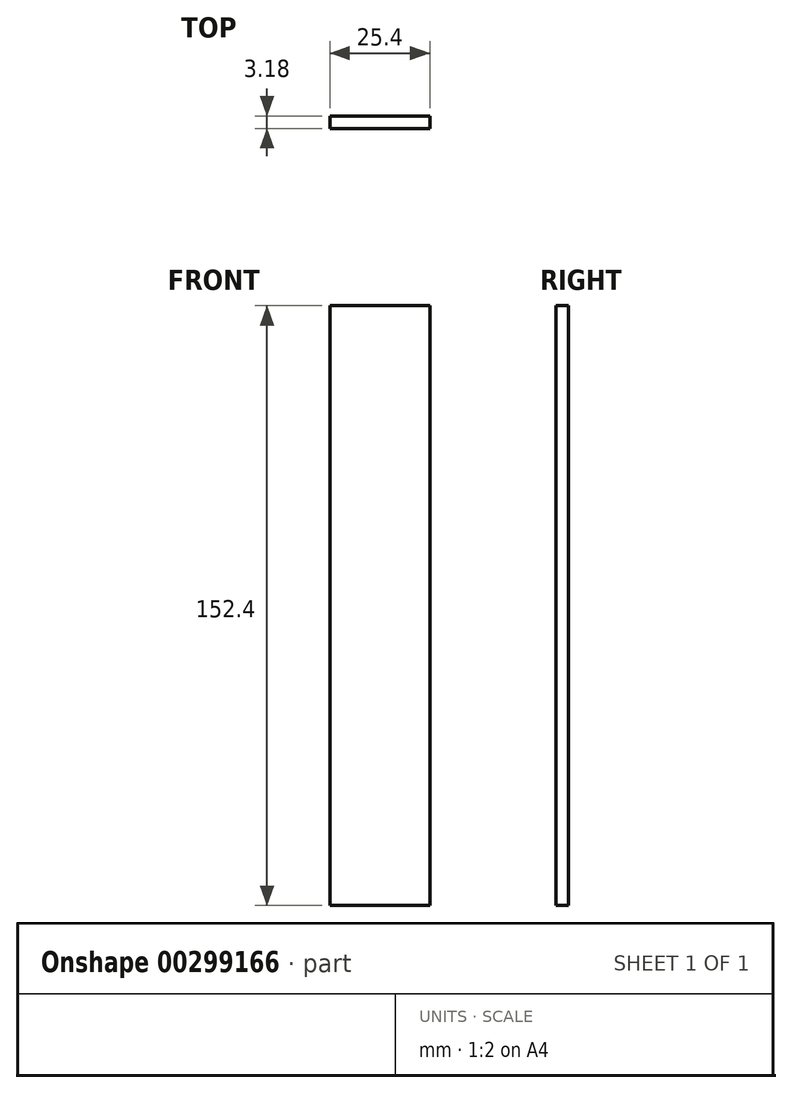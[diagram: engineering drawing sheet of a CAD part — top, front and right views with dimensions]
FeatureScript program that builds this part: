
annotation { "Feature Type Name" : "Feature", "Feature Type Description" : "" }
export const myFeature = defineFeature(function(context is Context, id is Id, definition is map)
    precondition{}
    {
        {
            var Q0;
            Q0=qCreatedBy(makeId("Front.planeOp"),FACE);
            var sketch = newSketch(context, id + "F0", { "sketchPlane" : qUnion([Q0])});
            skLineSegment(sketch, "E0.bottom", {"start": v(-12.7, 76.2) * mm, "end": v(12.7, 76.2) * mm});
            skLineSegment(sketch, "E0.top", {"start": v(-12.7, -76.2) * mm, "end": v(12.7, -76.2) * mm});
            skLineSegment(sketch, "E0.left", {"start": v(-12.7, 76.2) * mm, "end": v(-12.7, -76.2) * mm});
            skLineSegment(sketch, "E0.right", {"start": v(12.7, 76.2) * mm, "end": v(12.7, -76.2) * mm});
            skPoint(sketch, "E0.middle", {"position": v(0, 0) * mm});
            skSolve(sketch);
        }
        {
            var Q0;
            Q0 = qSketchRegion(id + "F0", true);
            extrude(context, id + "F1", {"entities" : qUnion([Q0]), "endBound" : BoundingType.SYMMETRIC, "depth" : 3.17 * mm});
        }
    });
